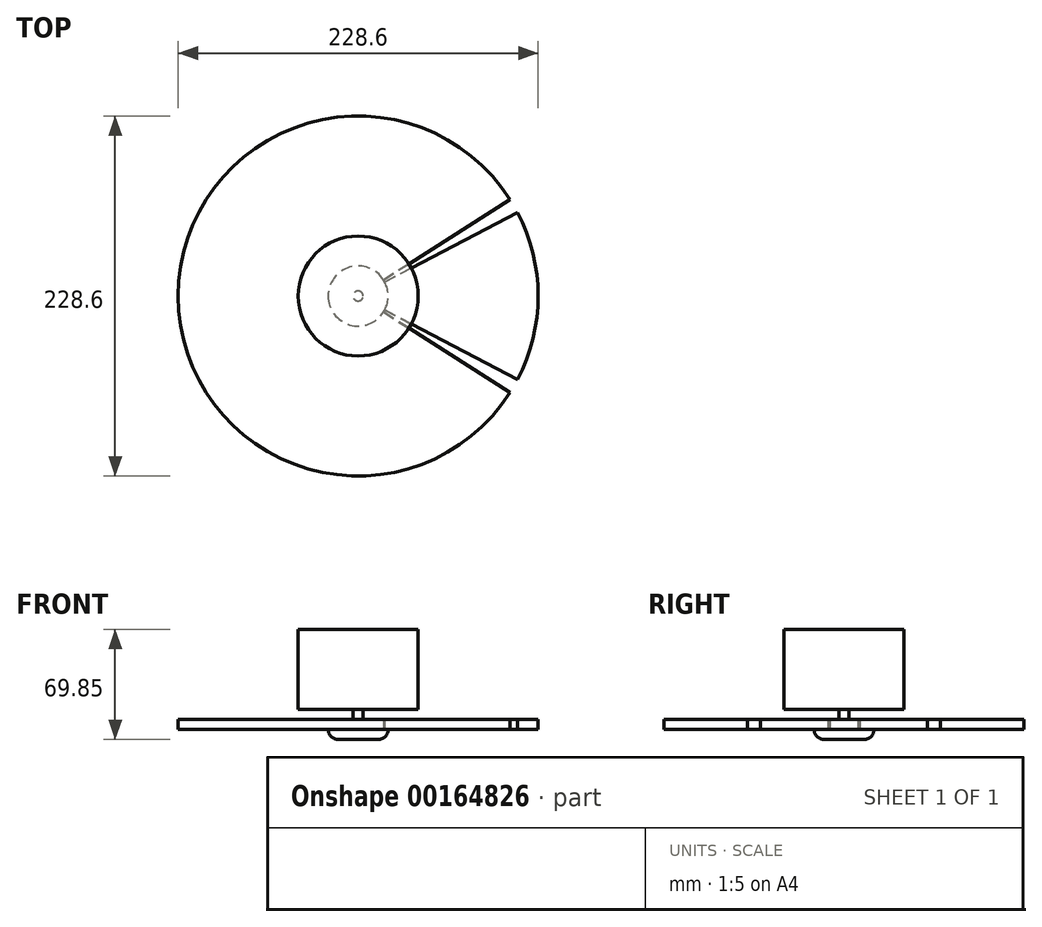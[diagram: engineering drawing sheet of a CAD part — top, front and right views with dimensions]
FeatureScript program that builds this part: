
annotation { "Feature Type Name" : "Feature", "Feature Type Description" : "" }
export const myFeature = defineFeature(function(context is Context, id is Id, definition is map)
    precondition{}
    {
        {
            var Q0;
            Q0=qCreatedBy(makeId("Top.planeOp"),FACE);
            var sketch = newSketch(context, id + "F0", { "sketchPlane" : qUnion([Q0])});
            skCircle(sketch, "E0", {"center": v(0, 0) * mm, "radius": 38.1 * mm});
            skSolve(sketch);
        }
        {
            var Q0;
            Q0 = qSketchRegion(id + "F0", true);
            extrude(context, id + "F1", {"entities" : qUnion([Q0]), "depth" : 50.8 * mm});
        }
        {
            var Q0;
            Q0=makeQuery(id+"F1.opExtrude","CAP_FACE",FACE,{"disambiguationData":[OSD([sQuery(id+"F0.wireOp",EDGE,"E0")])],"isStart":true});
            var sketch = newSketch(context, id + "F2", { "sketchPlane" : qUnion([Q0])});
            skCircle(sketch, "E1", {"center": v(0, 0) * mm, "radius": 3.18 * mm});
            skSolve(sketch);
        }
        {
            var Q0;
            Q0 = qSketchRegion(id + "F2", true);
            extrude(context, id + "F3", {"entities" : qUnion([Q0]), "operationType" : NewBodyOperationType.ADD, "depth" : 6.35 * mm});
        }
        {
            var Q0;
            Q0=makeQuery(id+"F3.opExtrude","CAP_FACE",FACE,{"disambiguationData":[OSD([sQuery(id+"F2.wireOp",EDGE,"E1")])],"isStart":false});
            var sketch = newSketch(context, id + "F4", { "sketchPlane" : qUnion([Q0])});
            skCircle(sketch, "E2", {"center": v(0, 0) * mm, "radius": 114.3 * mm});
            skSolve(sketch);
        }
        {
            var Q0;
            Q0 = qSketchRegion(id + "F4", true);
            extrude(context, id + "F5", {"entities" : qUnion([Q0]), "operationType" : NewBodyOperationType.ADD, "depth" : 6.35 * mm});
        }
        {
            var Q0;
            Q0=makeQuery(id+"F5.opExtrude","CAP_FACE",FACE,{"disambiguationData":[OSD([sQuery(id+"F4.wireOp",EDGE,"E2")])],"isStart":false});
            var sketch = newSketch(context, id + "F6", { "sketchPlane" : qUnion([Q0])});
            skArc(sketch, "E3", {"start": v(16.88, -8.83) * mm, "mid": v(19.05, 0) * mm, "end": v(16.88, 8.83) * mm, "construction": true});
            skArc(sketch, "E4", {"start": v(101.28, -52.98) * mm, "mid": v(114.3, 0) * mm, "end": v(101.28, 52.98) * mm});
            skLineSegment(sketch, "E5", {"start": v(0, 0) * mm, "end": v(19.05, 0) * mm, "construction": true});
            skLineSegment(sketch, "E6", {"start": v(19.05, 0) * mm, "end": v(114.3, 0) * mm, "construction": true});
            skLineSegment(sketch, "E7", {"start": v(16.88, 8.83) * mm, "end": v(101.28, 52.98) * mm});
            skLineSegment(sketch, "E8", {"start": v(16.88, -8.83) * mm, "end": v(101.28, -52.98) * mm});
            skArc(sketch, "E9", {"start": v(16.09, -10.2) * mm, "mid": v(16.5, -9.52) * mm, "end": v(16.88, -8.83) * mm});
            skLineSegment(sketch, "E10", {"start": v(16.09, -10.2) * mm, "end": v(16.88, -8.83) * mm, "construction": true});
            skLineSegment(sketch, "E11", {"start": v(0, 0) * mm, "end": v(16.09, -10.2) * mm, "construction": true});
            skLineSegment(sketch, "E12", {"start": v(16.09, -10.2) * mm, "end": v(96.52, -61.22) * mm});
            skArc(sketch, "E13", {"start": v(96.52, -61.22) * mm, "mid": v(98.99, -57.15) * mm, "end": v(101.28, -52.98) * mm});
            skLineSegment(sketch, "E14", {"start": v(16.88, -8.83) * mm, "end": v(0, 0) * mm, "construction": true});
            skLineSegment(sketch, "E15", {"start": v(0, 0) * mm, "end": v(98.99, -57.15) * mm, "construction": true});
            skArc(sketch, "E16", {"start": v(16.88, 8.83) * mm, "mid": v(16.5, 9.52) * mm, "end": v(16.09, 10.2) * mm});
            skArc(sketch, "E17", {"start": v(101.28, 52.98) * mm, "mid": v(98.99, 57.15) * mm, "end": v(96.52, 61.22) * mm});
            skLineSegment(sketch, "E18", {"start": v(0, 0) * mm, "end": v(98.99, 57.15) * mm, "construction": true});
            skLineSegment(sketch, "E19", {"start": v(16.88, 8.83) * mm, "end": v(16.09, 10.2) * mm, "construction": true});
            skLineSegment(sketch, "E20", {"start": v(16.09, 10.2) * mm, "end": v(96.52, 61.22) * mm});
            skLineSegment(sketch, "E21", {"start": v(0, 0) * mm, "end": v(16.88, 8.83) * mm, "construction": true});
            skLineSegment(sketch, "E22", {"start": v(16.09, 10.2) * mm, "end": v(0, 0) * mm, "construction": true});
            skSolve(sketch);
        }
        {
            var Q0;
            Q0 = qSketchRegion(id + "F6", true);
            var Q1;
            Q1=makeQuery(id+"F5.opExtrude","CAP_FACE",FACE,{"disambiguationData":[OSD([sQuery(id+"F4.wireOp",EDGE,"E2")])],"isStart":true});
            extrude(context, id + "F7", {"entities" : qUnion([Q0]), "operationType" : NewBodyOperationType.REMOVE, "endBound" : BoundingType.UP_TO_SURFACE, "oppositeDirection" : true, "endBoundEntityFace" : qUnion([Q1]), "depth" : 25.4 * mm});
        }
        {
            var Q0;
            Q0=makeQuery(id+"F5.opExtrude","CAP_FACE",FACE,{"disambiguationData":[OSD([sQuery(id+"F4.wireOp",EDGE,"E2")])],"isStart":false});
            var sketch = newSketch(context, id + "F8", { "sketchPlane" : qUnion([Q0])});
            skCircle(sketch, "E23", {"center": v(0, 0) * mm, "radius": 19.05 * mm});
            skSolve(sketch);
        }
        {
            var Q0;
            Q0 = qSketchRegion(id + "F8", true);
            extrude(context, id + "F9", {"entities" : qUnion([Q0]), "operationType" : NewBodyOperationType.ADD, "depth" : 6.35 * mm});
        }
        {
            var Q0;
            Q0=makeQuery(id+"F9.opExtrude","CAP_EDGE",EDGE,{"disambiguationData":[OSD([sQuery(id+"F8.wireOp",EDGE,"E23")])],"isStart":false});
            fillet(context, id + "F10", {"entities" : qUnion([Q0]), "radius" : 6.35 * mm, "tangentPropagation" : true, "allowEdgeOverflow" : false});
        }
    });
